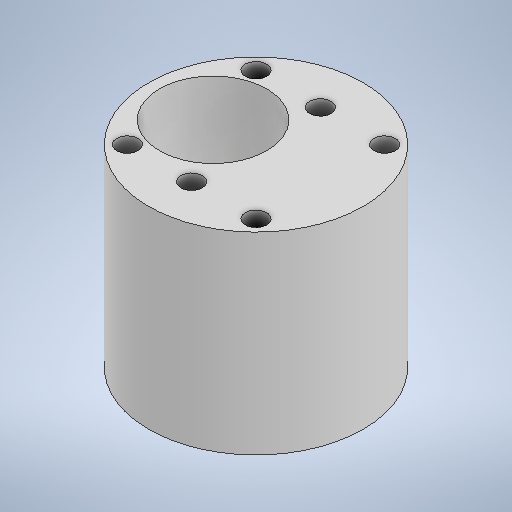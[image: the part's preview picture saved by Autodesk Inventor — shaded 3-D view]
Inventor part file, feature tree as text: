
AUTODESK INVENTOR PART (.ipt)
format: ipt  version: 2025.1 (Build 291241000, 241)  size: 233,472 bytes
history: native  units: mm
features: extrude x2, sketch x2
ambient origin geometry x8: Origin, YZ Plane, XZ Plane, XY Plane, X Axis, Y Axis, Z Axis, Center Point
bodies: Solid1 (feature_tree)
feature tree (4):
  extrude  "Extrusion1"  Depth=2.0mm
  extrude  "Extrusion2"  Depth=6.0mm
  sketch  "Sketch1"  dims[d0=20.0mm d2=2.0mm]
  sketch  "Sketch2"  dims[d3=12.0mm d4=6.0mm d5=12.0mm d6=6.0mm d7=6.0mm d8=2.0mm d9=18.0mm d10=0.0mm d11=10.0mm d12=4.0mm d13=18.0mm d14=0.0mm]
